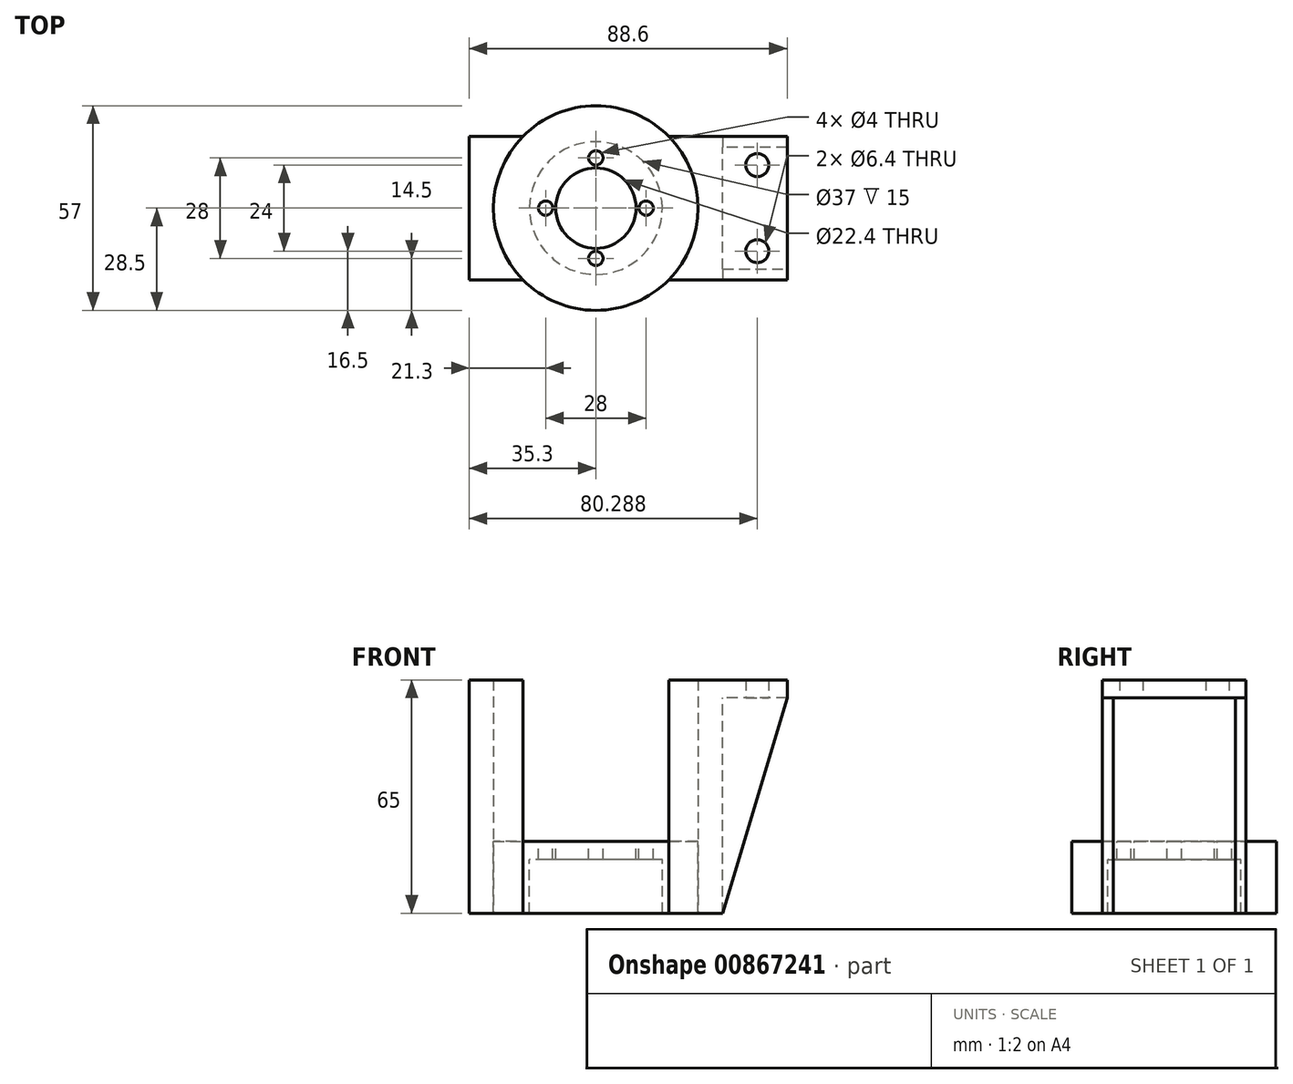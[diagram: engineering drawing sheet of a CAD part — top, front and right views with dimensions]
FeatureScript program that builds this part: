
annotation { "Feature Type Name" : "Feature", "Feature Type Description" : "" }
export const myFeature = defineFeature(function(context is Context, id is Id, definition is map)
    precondition{}
    {
        {
            var Q0;
            Q0=qCreatedBy(makeId("Top.planeOp"),FACE);
            var sketch = newSketch(context, id + "F0", { "sketchPlane" : qUnion([Q0])});
            skCircle(sketch, "E0", {"center": v(0, 0) * mm, "radius": 18.5 * mm});
            skCircle(sketch, "E1", {"center": v(0, 0) * mm, "radius": 28.5 * mm});
            skSolve(sketch);
        }
        {
            var Q0;
            Q0=makeQuery(id+"F0.imprint","IMPRINT",FACE,{"disambiguationData":[TD([[makeQuery(id+"F0.imprint","IMPRINT",EDGE,{"derivedFrom":sQuery(id+"F0.wireOp",EDGE,"E0")}),-1.0]])]});
            extrude(context, id + "F1", {"entities" : qUnion([Q0]), "oppositeDirection" : true, "depth" : 15 * mm, "offsetDistance" : 25 * mm});
        }
        {
            var Q0;
            Q0=makeQuery(id+"F1.opExtrude","CAP_FACE",FACE,{"disambiguationData":[OSD([sQuery(id+"F0.wireOp",EDGE,"E0"),sQuery(id+"F0.wireOp",EDGE,"E1")])],"isStart":true});
            var sketch = newSketch(context, id + "F2", { "sketchPlane" : qUnion([Q0])});
            skCircle(sketch, "E2", {"center": v(0, 0) * mm, "radius": 28.5 * mm});
            skSolve(sketch);
        }
        {
            var Q0;
            Q0=makeQuery(id+"F2.imprint","IMPRINT",FACE,{"disambiguationData":[TD([[makeQuery(id+"F2.imprint","IMPRINT",EDGE,{"derivedFrom":sQuery(id+"F2.wireOp",EDGE,"E2")}),1.0]])]});
            var Q1;
            Q1=makeQuery(id+"F2.imprint","IMPRINT",FACE,{"disambiguationData":[TD([[makeQuery(id+"F2.imprint","IMPRINT",EDGE,{"derivedFrom":makeQuery(id+"F1.opExtrude","CAP_EDGE",EDGE,{"disambiguationData":[OSD([sQuery(id+"F0.wireOp",EDGE,"E0")])],"isStart":true})}),1.0]])]});
            extrude(context, id + "F3", {"entities" : qUnion([Q0, Q1]), "operationType" : NewBodyOperationType.ADD, "depth" : 5 * mm, "offsetDistance" : 25 * mm});
        }
        {
            var Q0;
            Q0=makeQuery(id+"F3.opExtrude","CAP_FACE",FACE,{"disambiguationData":[OSD([sQuery(id+"F2.wireOp",EDGE,"E2")])],"isStart":false});
            var sketch = newSketch(context, id + "F4", { "sketchPlane" : qUnion([Q0])});
            skCircle(sketch, "E3", {"center": v(0, 0) * mm, "radius": 11.2 * mm});
            skCircle(sketch, "E4", {"center": v(0, 0) * mm, "radius": 14 * mm, "construction": true});
            skCircle(sketch, "E5", {"center": v(0, 14) * mm, "radius": 2 * mm});
            skCircle(sketch, "E6.1.0", {"center": v(-14, 0) * mm, "radius": 2 * mm});
            skCircle(sketch, "E6.2.0", {"center": v(0, -14) * mm, "radius": 2 * mm});
            skCircle(sketch, "E6.3.0", {"center": v(14, 0) * mm, "radius": 2 * mm});
            skSolve(sketch);
        }
        {
            var Q0;
            Q0=makeQuery(id+"F4.imprint","IMPRINT",FACE,{"disambiguationData":[TD([[makeQuery(id+"F4.imprint","IMPRINT",EDGE,{"derivedFrom":sQuery(id+"F4.wireOp",EDGE,"E5")}),1.0]])]});
            var Q1;
            Q1=makeQuery(id+"F4.imprint","IMPRINT",FACE,{"disambiguationData":[TD([[makeQuery(id+"F4.imprint","IMPRINT",EDGE,{"derivedFrom":sQuery(id+"F4.wireOp",EDGE,"E3")}),1.0]])]});
            var Q2;
            Q2=makeQuery(id+"F4.imprint","IMPRINT",FACE,{"disambiguationData":[TD([[makeQuery(id+"F4.imprint","IMPRINT",EDGE,{"derivedFrom":sQuery(id+"F4.wireOp",EDGE,"E6.1.0")}),1.0]])]});
            var Q3;
            Q3=makeQuery(id+"F4.imprint","IMPRINT",FACE,{"disambiguationData":[TD([[makeQuery(id+"F4.imprint","IMPRINT",EDGE,{"derivedFrom":sQuery(id+"F4.wireOp",EDGE,"E6.2.0")}),1.0]])]});
            var Q4;
            Q4=makeQuery(id+"F4.imprint","IMPRINT",FACE,{"disambiguationData":[TD([[makeQuery(id+"F4.imprint","IMPRINT",EDGE,{"derivedFrom":sQuery(id+"F4.wireOp",EDGE,"E6.3.0")}),1.0]])]});
            extrude(context, id + "F5", {"entities" : qUnion([Q0, Q1, Q2, Q3, Q4]), "operationType" : NewBodyOperationType.REMOVE, "oppositeDirection" : true, "depth" : 25 * mm, "offsetDistance" : 25 * mm});
        }
        {
            var Q0;
            Q0=makeQuery(id+"F1.opExtrude","CAP_FACE",FACE,{"disambiguationData":[OSD([sQuery(id+"F0.wireOp",EDGE,"E0"),sQuery(id+"F0.wireOp",EDGE,"E1")])],"isStart":false});
            var sketch = newSketch(context, id + "F6", { "sketchPlane" : qUnion([Q0])});
            skLineSegment(sketch, "E7.bottom", {"start": v(20.3, 20) * mm, "end": v(35.3, 20) * mm});
            skLineSegment(sketch, "E7.top", {"start": v(20.3, -20) * mm, "end": v(35.3, -20) * mm});
            skLineSegment(sketch, "E7.right", {"start": v(35.3, 20) * mm, "end": v(35.3, -20) * mm});
            skLineSegment(sketch, "E8.1.0", {"start": v(-20.3, -20) * mm, "end": v(-35.3, -20) * mm});
            skLineSegment(sketch, "E8.1.1", {"start": v(-35.3, -20) * mm, "end": v(-35.3, 20) * mm});
            skLineSegment(sketch, "E8.1.2", {"start": v(-20.3, 20) * mm, "end": v(-35.3, 20) * mm});
            skPoint(sketch, "E8.center", {"position": v(0, 0) * mm});
            skSolve(sketch);
        }
        {
            var Q0;
            {var subQ0=sQuery(id+"F6.wireOp",EDGE,"E8.1.0");Q0=makeQuery(id+"F6.imprint","IMPRINT",FACE,{"disambiguationData":[TD([[makeQuery(id+"F6.imprint","IMPRINT",EDGE,{"derivedFrom":subQ0}),-1.0]])]});}
            var Q1;
            {var subQ0=sQuery(id+"F6.wireOp",EDGE,"E8.2.0");Q1=makeQuery(id+"F6.imprint","IMPRINT",FACE,{"disambiguationData":[TD([[makeQuery(id+"F6.imprint","IMPRINT",EDGE,{"derivedFrom":subQ0}),-1.0]])]});}
            var Q2;
            {var subQ0=sQuery(id+"F6.wireOp",EDGE,"E7.bottom");Q2=makeQuery(id+"F6.imprint","IMPRINT",FACE,{"disambiguationData":[TD([[makeQuery(id+"F6.imprint","IMPRINT",EDGE,{"derivedFrom":subQ0}),-1.0]])]});}
            extrude(context, id + "F7", {"entities" : qUnion([Q0, Q1, Q2]), "oppositeDirection" : true, "depth" : 65 * mm, "offsetDistance" : 25 * mm});
        }
        {
            var Q0;
            Q0=makeQuery(id+"F7.opExtrude","SWEPT_FACE",FACE,{"disambiguationData":[OSD([sQuery(id+"F6.wireOp",EDGE,"E7.right")])]});
            var sketch = newSketch(context, id + "F8", { "sketchPlane" : qUnion([Q0])});
            skLineSegment(sketch, "E9.bottom", {"start": v(-20, 50) * mm, "end": v(20, 50) * mm});
            skLineSegment(sketch, "E9.top", {"start": v(-20, 45) * mm, "end": v(20, 45) * mm});
            skLineSegment(sketch, "E9.left", {"start": v(-20, 50) * mm, "end": v(-20, 45) * mm});
            skLineSegment(sketch, "E9.right", {"start": v(20, 50) * mm, "end": v(20, 45) * mm});
            skSolve(sketch);
        }
        {
            var Q0;
            Q0=makeQuery(id+"F8.imprint","IMPRINT",FACE,{"disambiguationData":[TD([[makeQuery(id+"F8.imprint","IMPRINT",EDGE,{"derivedFrom":sQuery(id+"F8.wireOp",EDGE,"E9.bottom")}),-1.0]])]});
            extrude(context, id + "F9", {"entities" : qUnion([Q0]), "operationType" : NewBodyOperationType.ADD, "depth" : 18 * mm, "offsetDistance" : 25 * mm});
        }
        {
            var Q0;
            Q0=makeQuery(id+"F9.opExtrude","SWEPT_FACE",FACE,{"disambiguationData":[OSD([sQuery(id+"F8.wireOp",EDGE,"E9.top")])]});
            var sketch = newSketch(context, id + "F10", { "sketchPlane" : qUnion([Q0])});
            skCircle(sketch, "E10", {"center": v(44.99, 12) * mm, "radius": 3.2 * mm});
            skCircle(sketch, "E11", {"center": v(44.99, -12) * mm, "radius": 3.2 * mm});
            skSolve(sketch);
        }
        {
            var Q0;
            Q0=makeQuery(id+"F10.imprint","IMPRINT",FACE,{"disambiguationData":[TD([[makeQuery(id+"F10.imprint","IMPRINT",EDGE,{"derivedFrom":sQuery(id+"F10.wireOp",EDGE,"E10")}),1.0]])]});
            var Q1;
            Q1=makeQuery(id+"F10.imprint","IMPRINT",FACE,{"disambiguationData":[TD([[makeQuery(id+"F10.imprint","IMPRINT",EDGE,{"derivedFrom":sQuery(id+"F10.wireOp",EDGE,"E11")}),1.0]])]});
            extrude(context, id + "F11", {"entities" : qUnion([Q0, Q1]), "operationType" : NewBodyOperationType.REMOVE, "oppositeDirection" : true, "depth" : 25 * mm, "offsetDistance" : 25 * mm});
        }
        {
            var Q0;
            Q0=makeQuery(id+"F9.opExtrude","SWEPT_FACE",FACE,{"disambiguationData":[OSD([sQuery(id+"F8.wireOp",EDGE,"E9.top")])]});
            var sketch = newSketch(context, id + "F12", { "sketchPlane" : qUnion([Q0])});
            skLineSegment(sketch, "E12.bottom", {"start": v(35.3, 20) * mm, "end": v(53.3, 20) * mm});
            skLineSegment(sketch, "E12.top", {"start": v(35.3, 17) * mm, "end": v(53.3, 17) * mm});
            skLineSegment(sketch, "E12.left", {"start": v(35.3, 20) * mm, "end": v(35.3, 17) * mm});
            skLineSegment(sketch, "E12.right", {"start": v(53.3, 20) * mm, "end": v(53.3, 17) * mm});
            skLineSegment(sketch, "E13.bottom", {"start": v(53.3, -20) * mm, "end": v(35.3, -20) * mm});
            skLineSegment(sketch, "E13.top", {"start": v(53.3, -17) * mm, "end": v(35.3, -17) * mm});
            skLineSegment(sketch, "E13.left", {"start": v(53.3, -20) * mm, "end": v(53.3, -17) * mm});
            skLineSegment(sketch, "E13.right", {"start": v(35.3, -20) * mm, "end": v(35.3, -17) * mm});
            skSolve(sketch);
        }
        {
            var Q0;
            Q0=makeQuery(id+"F12.imprint","IMPRINT",FACE,{"disambiguationData":[TD([[makeQuery(id+"F12.imprint","IMPRINT",EDGE,{"derivedFrom":sQuery(id+"F12.wireOp",EDGE,"E12.bottom")}),1.0]])]});
            var Q1;
            Q1=makeQuery(id+"F12.imprint","IMPRINT",FACE,{"disambiguationData":[TD([[makeQuery(id+"F12.imprint","IMPRINT",EDGE,{"derivedFrom":sQuery(id+"F12.wireOp",EDGE,"E13.bottom")}),-1.0]])]});
            extrude(context, id + "F13", {"entities" : qUnion([Q0, Q1]), "operationType" : NewBodyOperationType.ADD, "depth" : 60 * mm, "offsetDistance" : 25 * mm});
        }
        {
            var Q0;
            Q0=makeQuery(id+"F13.opExtrude","CAP_EDGE",EDGE,{"disambiguationData":[OSD([sQuery(id+"F12.wireOp",EDGE,"E12.right")])],"isStart":false});
            var Q1;
            Q1=makeQuery(id+"F13.opExtrude","CAP_EDGE",EDGE,{"disambiguationData":[OSD([sQuery(id+"F12.wireOp",EDGE,"E13.left")])],"isStart":false});
            chamfer(context, id + "F14", {"entities" : qUnion([Q0, Q1]), "chamferType" : ChamferType.TWO_OFFSETS, "width1" : 60 * mm, "oppositeDirection" : false, "width2" : 18 * mm, "tangentPropagation" : true});
        }
    });
